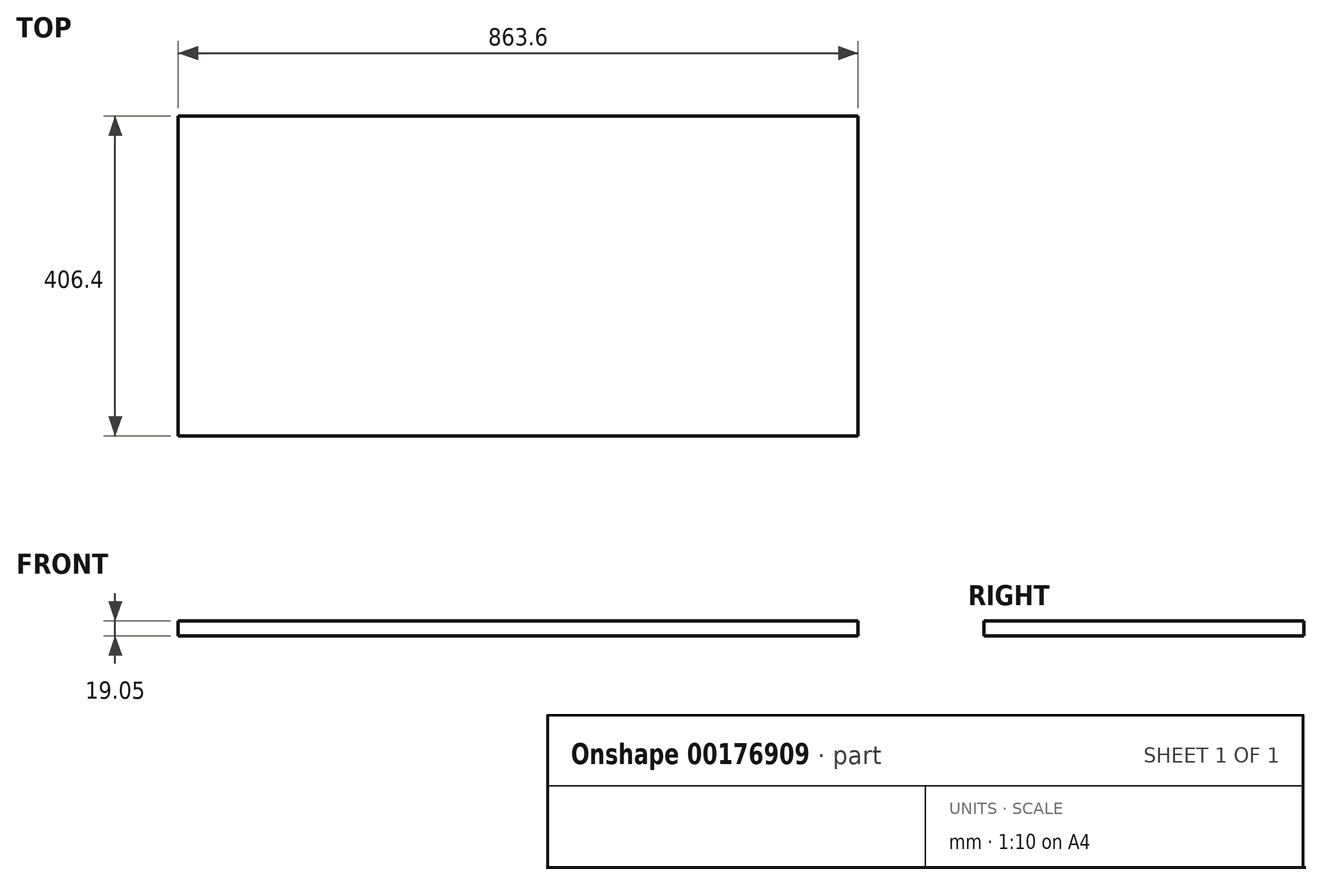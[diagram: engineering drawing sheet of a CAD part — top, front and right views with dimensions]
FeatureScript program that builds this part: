
annotation { "Feature Type Name" : "Feature", "Feature Type Description" : "" }
export const myFeature = defineFeature(function(context is Context, id is Id, definition is map)
    precondition{}
    {
        {
            var Q0;
            Q0=qCreatedBy(makeId("Top.planeOp"),FACE);
            var sketch = newSketch(context, id + "F0", { "sketchPlane" : qUnion([Q0])});
            skLineSegment(sketch, "E0.bottom", {"start": v(-439.93, 208.04) * mm, "end": v(423.67, 208.04) * mm});
            skLineSegment(sketch, "E0.top", {"start": v(-439.93, -198.36) * mm, "end": v(423.67, -198.36) * mm});
            skLineSegment(sketch, "E0.left", {"start": v(-439.93, 208.04) * mm, "end": v(-439.93, -198.36) * mm});
            skLineSegment(sketch, "E0.right", {"start": v(423.67, 208.04) * mm, "end": v(423.67, -198.36) * mm});
            skLineSegment(sketch, "E1.top", {"start": v(-439.93, 227.1) * mm, "end": v(423.67, 227.1) * mm});
            skLineSegment(sketch, "E1.left", {"start": v(-439.93, 208.04) * mm, "end": v(-439.93, 227.1) * mm});
            skLineSegment(sketch, "E2", {"start": v(423.67, 208.04) * mm, "end": v(423.67, 227.1) * mm});
            skLineSegment(sketch, "E3.bottom", {"start": v(-439.93, 227.1) * mm, "end": v(-458.98, 227.1) * mm});
            skLineSegment(sketch, "E3.top", {"start": v(-439.93, -197.55) * mm, "end": v(-458.98, -197.55) * mm});
            skLineSegment(sketch, "E3.left", {"start": v(-439.93, 227.1) * mm, "end": v(-439.93, -197.55) * mm});
            skLineSegment(sketch, "E3.right", {"start": v(-458.98, 227.1) * mm, "end": v(-458.98, -197.55) * mm});
            skLineSegment(sketch, "E4.bottom", {"start": v(423.67, 227.1) * mm, "end": v(442.72, 227.1) * mm});
            skLineSegment(sketch, "E4.top", {"start": v(423.67, -198.36) * mm, "end": v(442.72, -198.36) * mm});
            skLineSegment(sketch, "E4.left", {"start": v(423.67, 227.1) * mm, "end": v(423.67, -198.36) * mm});
            skLineSegment(sketch, "E4.right", {"start": v(442.72, 227.1) * mm, "end": v(442.72, -198.36) * mm});
            skSolve(sketch);
        }
        {
            var Q0;
            {var subQ3=sQuery(id+"F0.wireOp",EDGE,"E0.top");Q0=makeQuery(id+"F0.imprint","IMPRINT",FACE,{"disambiguationData":[TD([[makeQuery(id+"F0.imprint","IMPRINT",EDGE,{"derivedFrom":subQ3}),1.0]])]});}
            extrude(context, id + "F1", {"entities" : qUnion([Q0]), "depth" : 19.05 * mm});
        }
    });
